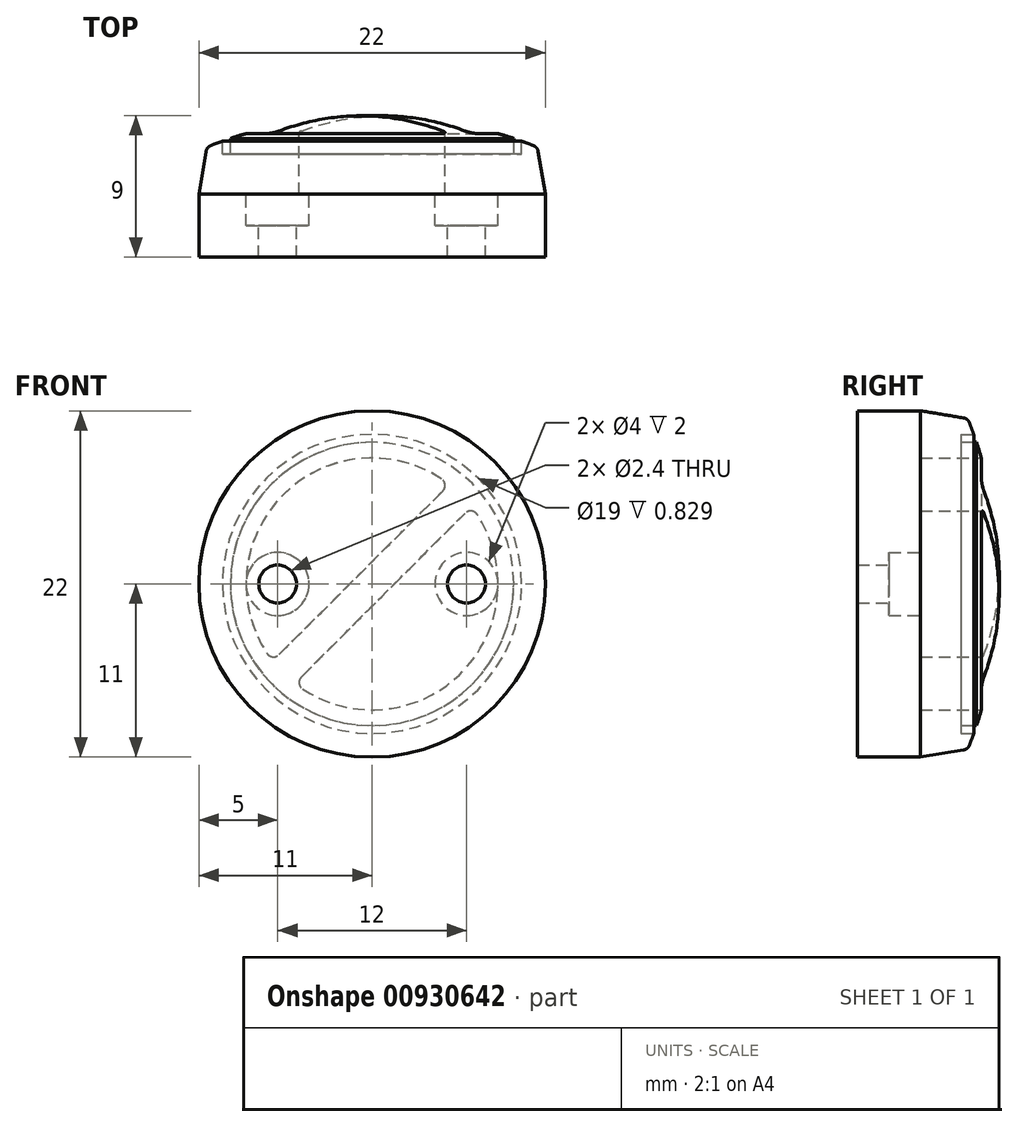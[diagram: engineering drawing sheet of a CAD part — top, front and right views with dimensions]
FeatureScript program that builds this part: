
annotation { "Feature Type Name" : "Feature", "Feature Type Description" : "" }
export const myFeature = defineFeature(function(context is Context, id is Id, definition is map)
    precondition{}
    {
        {
            var Q0;
            Q0=qCreatedBy(makeId("Top.planeOp"),FACE);
            var sketch = newSketch(context, id + "F0", { "sketchPlane" : qUnion([Q0])});
            skLineSegment(sketch, "E0", {"start": v(0, 0) * mm, "end": v(11, 0) * mm});
            skLineSegment(sketch, "E1", {"start": v(0, 9) * mm, "end": v(0, 0) * mm});
            skArc(sketch, "E2", {"start": v(10.5, 7) * mm, "mid": v(10, 7.2) * mm, "end": v(9.5, 7.37) * mm});
            skLineSegment(sketch, "E3", {"start": v(0, 9) * mm, "end": v(11, 9) * mm, "construction": true});
            skLineSegment(sketch, "E4", {"start": v(11, 9) * mm, "end": v(11, 0) * mm, "construction": true});
            skLineSegment(sketch, "E5", {"start": v(9, 7.54) * mm, "end": v(9, 6.54) * mm});
            skLineSegment(sketch, "E6", {"start": v(9, 6.54) * mm, "end": v(9.5, 6.54) * mm});
            skLineSegment(sketch, "E7", {"start": v(9.5, 6.54) * mm, "end": v(9.5, 7.37) * mm});
            skArc(sketch, "E8.trimOffspring", {"start": v(9, 7.54) * mm, "mid": v(4.56, 8.63) * mm, "end": v(0, 9) * mm});
            skLineSegment(sketch, "E9", {"start": v(11, 0) * mm, "end": v(11, 4) * mm});
            skLineSegment(sketch, "E10", {"start": v(11, 4) * mm, "end": v(10.5, 7) * mm});
            skSolve(sketch);
        }
        {
            var Q0;
            Q0=qSketchRegion(id+"F0",true);
            var Q1;
            Q1=sQuery(id+"F0.wireOp",EDGE,"E1");
            revolve(context, id + "F1", {"entities" : qUnion([Q0]), "axis" : qUnion([Q1]), "revolveType" : RevolveType.FULL});
        }
        {
            var Q0;
            Q0=makeQuery(id+"F1.opRevolve","SWEPT_EDGE",EDGE,{"disambiguationData":[OSD([sQuery(id+"F0.wireOp",EDGE,"E2"),sQuery(id+"F0.wireOp",EDGE,"E10")])]});
            fillet(context, id + "F2", {"entities" : qUnion([Q0]), "radius" : 0.5 * mm, "tangentPropagation" : true, "allowEdgeOverflow" : false});
        }
        {
            var Q0;
            Q0=qCreatedBy(makeId("Front.planeOp"),FACE);
            cPlane(context, id + "F3", {"entities" : qUnion([Q0]), "cplaneType" : CPlaneType.OFFSET, "offset" : 9 * mm, "oppositeDirection" : true, "width" : 150 * mm, "height" : 150 * mm});
        }
        {
            var Q0;
            Q0=qCreatedBy(id+"F3.planeOp",FACE);
            var sketch = newSketch(context, id + "F4", { "sketchPlane" : qUnion([Q0])});
            skLineSegment(sketch, "E11", {"start": v(5.66, 5.66) * mm, "end": v(-5.66, -5.66) * mm, "construction": true});
            skLineSegment(sketch, "E12", {"start": v(6.32, 4.9) * mm, "end": v(-4.9, -6.32) * mm});
            skLineSegment(sketch, "E13", {"start": v(4.9, 6.32) * mm, "end": v(-6.32, -4.9) * mm});
            skArc(sketch, "E14", {"start": v(-4.9, -6.32) * mm, "mid": v(5.66, -5.66) * mm, "end": v(6.32, 4.9) * mm});
            skArc(sketch, "E15.trimOffspring", {"start": v(4.9, 6.32) * mm, "mid": v(-5.66, 5.66) * mm, "end": v(-6.32, -4.9) * mm});
            skSolve(sketch);
        }
        {
            var Q0;
            Q0=qSketchRegion(id+"F4",true);
            extrude(context, id + "F5", {"entities" : qUnion([Q0]), "operationType" : NewBodyOperationType.REMOVE, "depth" : 5 * mm, "offsetDistance" : 25 * mm});
        }
        {
            var Q0;
            Q0=makeQuery(id+"F5.boolean.opBoolean","COPY",EDGE,{"derivedFrom":makeQuery(id+"F5.opExtrude","SWEPT_EDGE",EDGE,{"disambiguationData":[OSD([sQuery(id+"F4.wireOp",EDGE,"E12"),sQuery(id+"F4.wireOp",EDGE,"9U1DXfUO-Rlwk-1aOU-0xu6-zXaTAB0kp4wo")])]})});
            var Q1;
            Q1=makeQuery(id+"F5.boolean.opBoolean","COPY",EDGE,{"derivedFrom":makeQuery(id+"F5.opExtrude","SWEPT_EDGE",EDGE,{"disambiguationData":[OSD([sQuery(id+"F4.wireOp",EDGE,"E13"),sQuery(id+"F4.wireOp",EDGE,"9U1DXfUO-Rlwk-1aOU-0xu6-zXaTAB0kp4wo")])]})});
            var Q2;
            Q2=makeQuery(id+"F5.boolean.opBoolean","COPY",EDGE,{"derivedFrom":makeQuery(id+"F5.opExtrude","SWEPT_EDGE",EDGE,{"disambiguationData":[OSD([sQuery(id+"F4.wireOp",EDGE,"E13"),sQuery(id+"F4.wireOp",EDGE,"kEzsly48-vxgy-kpaP-8O0y-I7d7fxUrVZxT")])]})});
            var Q3;
            Q3=makeQuery(id+"F5.boolean.opBoolean","COPY",EDGE,{"derivedFrom":makeQuery(id+"F5.opExtrude","SWEPT_EDGE",EDGE,{"disambiguationData":[OSD([sQuery(id+"F4.wireOp",EDGE,"E12"),sQuery(id+"F4.wireOp",EDGE,"kEzsly48-vxgy-kpaP-8O0y-I7d7fxUrVZxT")])]})});
            fillet(context, id + "F6", {"entities" : qUnion([Q0, Q1, Q2, Q3]), "radius" : 0.5 * mm, "tangentPropagation" : true, "allowEdgeOverflow" : false});
        }
        {
            var Q0;
            Q0=qCreatedBy(id+"F3.planeOp",FACE);
            var sketch = newSketch(context, id + "F7", { "sketchPlane" : qUnion([Q0])});
            skCircle(sketch, "E16", {"center": v(6, 0) * mm, "radius": 2 * mm});
            skCircle(sketch, "E17", {"center": v(-6, 0) * mm, "radius": 2 * mm});
            skSolve(sketch);
        }
        {
            var Q0;
            Q0=qSketchRegion(id+"F7",true);
            extrude(context, id + "F8", {"entities" : qUnion([Q0]), "operationType" : NewBodyOperationType.REMOVE, "depth" : 7 * mm, "offsetDistance" : 25 * mm});
        }
        {
            var Q0;
            Q0=makeQuery(id+"F8.boolean.opBoolean","COPY",FACE,{"derivedFrom":makeQuery(id+"F8.opExtrude","CAP_FACE",FACE,{"disambiguationData":[OSD([sQuery(id+"F7.wireOp",EDGE,"E16")])],"isStart":false})});
            var sketch = newSketch(context, id + "F9", { "sketchPlane" : qUnion([Q0])});
            skCircle(sketch, "E18", {"center": v(-6, 0) * mm, "radius": 1.2 * mm});
            skCircle(sketch, "E19", {"center": v(6, 0) * mm, "radius": 1.2 * mm});
            skSolve(sketch);
        }
        {
            var Q0;
            Q0=qSketchRegion(id+"F9",true);
            extrude(context, id + "F10", {"entities" : qUnion([Q0]), "operationType" : NewBodyOperationType.REMOVE, "oppositeDirection" : true, "depth" : 25 * mm, "offsetDistance" : 25 * mm});
        }
    });
